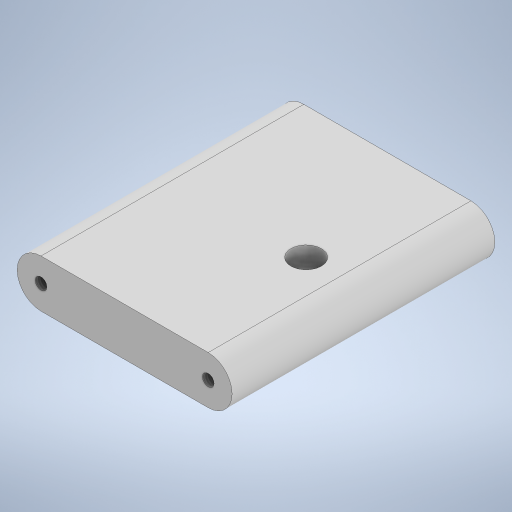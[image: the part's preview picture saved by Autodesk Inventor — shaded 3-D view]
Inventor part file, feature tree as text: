
AUTODESK INVENTOR PART (.ipt)
format: ipt  version: 2024.3 (Build 283343010, 343A)  size: 245,760 bytes
history: native  units: mm
features: sketch x5, hole x3, extrude x2, projected_geometry x2, other x1
ambient origin geometry x8: Origin, YZ Plane, XZ Plane, XY Plane, X Axis, Y Axis, Z Axis, Center Point
bodies: Body1 (feature_tree)
feature tree (13):
  other  "ソリッド1"
  extrude  "押し出し1"  Depth=45.0mm
  hole  "穴1"  [1 undecoded]
  hole  "穴2"  [1 undecoded]
  hole  "穴3"  [1 undecoded]
  extrude  "押し出し2"  Depth=5.0mm
  sketch  "スケッチ1"
  sketch  "スケッチ2"
  sketch  "スケッチ3"
  projected_geometry  "投影ループ1"
  sketch  "スケッチ4"
  sketch  "スケッチ5"
  projected_geometry  "投影ループ2"
note: 3 required parameter values undecoded (feature->parameter linkage not recoverable at this tier; creation-order binding heuristic only, values carry confidence <= 0.55)
